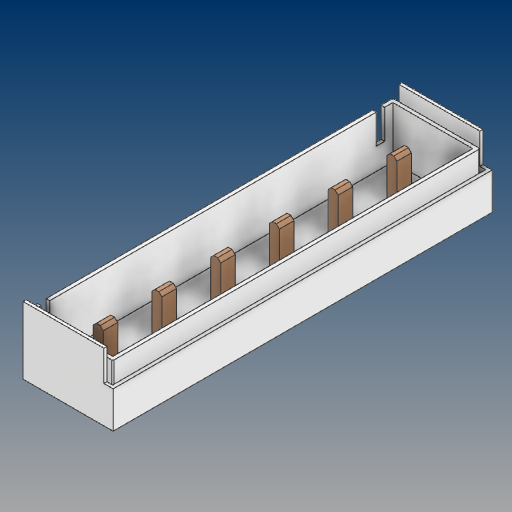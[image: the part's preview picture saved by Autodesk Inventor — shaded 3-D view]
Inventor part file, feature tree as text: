
AUTODESK INVENTOR PART (.ipt)
format: ipt  version: 2021 (Build 250183000, 183)  size: 171,520 bytes
history: native  units: mm
features: chamfer x1, other x1
ambient origin geometry x8: Origin, YZ Plane, XZ Plane, XY Plane, X Axis, Y Axis, Z Axis, Center Point
bodies: Solid1 (feature_tree), Solid2 (feature_tree)
feature tree (2):
  chamfer  "Chamfer2"  [1 undecoded]
  other  "Boss-Extrude4"
note: 1 required parameter value undecoded (feature->parameter linkage not recoverable at this tier; creation-order binding heuristic only, values carry confidence <= 0.55)
